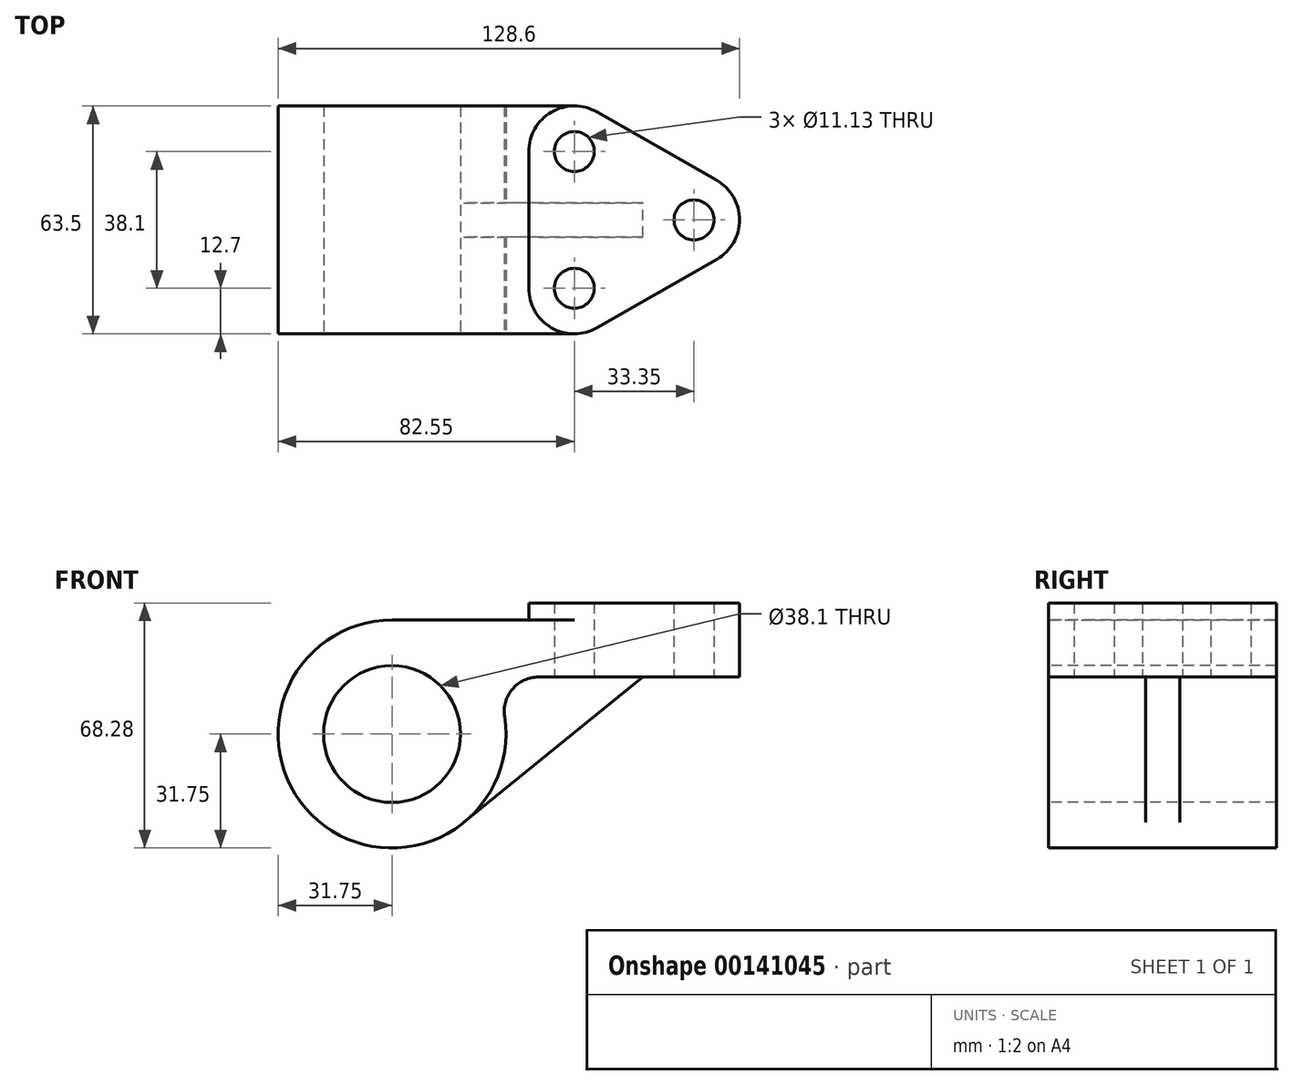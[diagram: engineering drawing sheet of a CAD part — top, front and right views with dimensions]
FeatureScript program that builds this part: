
annotation { "Feature Type Name" : "Feature", "Feature Type Description" : "" }
export const myFeature = defineFeature(function(context is Context, id is Id, definition is map)
    precondition{}
    {
        {
            var Q0;
            Q0=qCreatedBy(makeId("Front.planeOp"),FACE);
            var sketch = newSketch(context, id + "F0", { "sketchPlane" : qUnion([Q0])});
            skCircle(sketch, "E0", {"center": v(0, 0) * mm, "radius": 19.05 * mm});
            skCircle(sketch, "E1", {"center": v(0, 0) * mm, "radius": 31.75 * mm});
            skLineSegment(sketch, "E2", {"start": v(0, 31.75) * mm, "end": v(50.8, 31.75) * mm});
            skLineSegment(sketch, "E3", {"start": v(50.8, 31.75) * mm, "end": v(50.8, 15.87) * mm});
            skLineSegment(sketch, "E4", {"start": v(50.8, 15.87) * mm, "end": v(27.5, 15.87) * mm});
            skSolve(sketch);
        }
        {
            var Q0;
            Q0=qSketchRegion(id+"F0",true);
            extrude(context, id + "F1", {"entities" : qUnion([Q0]), "endBound" : BoundingType.SYMMETRIC, "oppositeDirection" : true, "depth" : 63.5 * mm});
        }
        {
            var Q0;
            Q0=makeQuery(id+"F1.opExtrude","SWEPT_FACE",FACE,{"disambiguationData":[OSD([sQuery(id+"F0.wireOp",EDGE,"E4")])]});
            var sketch = newSketch(context, id + "F2", { "sketchPlane" : qUnion([Q0])});
            skCircle(sketch, "E5", {"center": v(50.8, 19.05) * mm, "radius": 5.56 * mm});
            skCircle(sketch, "E6", {"center": v(50.8, -19.05) * mm, "radius": 5.56 * mm});
            skCircle(sketch, "E7", {"center": v(84.15, 0) * mm, "radius": 5.56 * mm});
            skLineSegment(sketch, "E8", {"start": v(50.8, 31.75) * mm, "end": v(27.5, 31.75) * mm, "construction": true});
            skLineSegment(sketch, "E9", {"start": v(27.5, 31.75) * mm, "end": v(27.5, -31.75) * mm, "construction": true});
            skLineSegment(sketch, "E10", {"start": v(27.5, -31.75) * mm, "end": v(50.8, -31.75) * mm, "construction": true});
            skLineSegment(sketch, "E11", {"start": v(50.8, -31.75) * mm, "end": v(50.8, 31.75) * mm, "construction": true});
            skArc(sketch, "E12", {"start": v(57.1, 30.08) * mm, "mid": v(44.42, 30.03) * mm, "end": v(38.1, 19.05) * mm});
            skArc(sketch, "E13", {"start": v(90.45, -11.03) * mm, "mid": v(96.85, 0) * mm, "end": v(90.45, 11.03) * mm});
            skArc(sketch, "E14", {"start": v(38.1, -19.05) * mm, "mid": v(44.42, -30.03) * mm, "end": v(57.1, -30.08) * mm});
            skLineSegment(sketch, "E15", {"start": v(57.1, 30.08) * mm, "end": v(90.45, 11.03) * mm});
            skLineSegment(sketch, "E16", {"start": v(90.45, -11.03) * mm, "end": v(57.1, -30.08) * mm});
            skLineSegment(sketch, "E17", {"start": v(38.1, 19.05) * mm, "end": v(38.1, -19.05) * mm});
            skSolve(sketch);
        }
        {
            var Q0;
            Q0=qSketchRegion(id+"F2",true);
            extrude(context, id + "F3", {"entities" : qUnion([Q0]), "operationType" : NewBodyOperationType.ADD, "oppositeDirection" : true, "depth" : 20.65 * mm});
        }
        {
            var Q0;
            Q0=makeQuery(id+"F1.opExtrude","SWEPT_EDGE",EDGE,{"disambiguationData":[OSD([sQuery(id+"F0.wireOp",EDGE,"E1"),sQuery(id+"F0.wireOp",EDGE,"E4")])]});
            fillet(context, id + "F4", {"entities" : qUnion([Q0]), "radius" : 9.52 * mm, "tangentPropagation" : true, "allowEdgeOverflow" : false});
        }
        {
            var Q0;
            Q0=qCreatedBy(makeId("Front.planeOp"),FACE);
            var sketch = newSketch(context, id + "F5", { "sketchPlane" : qUnion([Q0])});
            skLineSegment(sketch, "E18", {"start": v(69.85, 15.88) * mm, "end": v(20.03, -24.63) * mm});
            skArc(sketch, "E19.0", {"start": v(20.03, -24.63) * mm, "mid": v(29.64, -11.39) * mm, "end": v(31.37, 4.88) * mm});
            skArc(sketch, "E19.1", {"start": v(31.37, 4.88) * mm, "mid": v(33.55, 12.55) * mm, "end": v(40.78, 15.87) * mm});
            skLineSegment(sketch, "E19.2", {"start": v(50.8, 15.87) * mm, "end": v(40.78, 15.87) * mm});
            skLineSegment(sketch, "E19.3", {"start": v(57.1, 15.88) * mm, "end": v(50.8, 15.88) * mm});
            skLineSegment(sketch, "E19.4", {"start": v(57.1, 15.88) * mm, "end": v(69.85, 15.88) * mm});
            skPoint(sketch, "E20", {"position": v(20.03, -24.63) * mm});
            skPoint(sketch, "E21", {"position": v(69.85, 15.88) * mm});
            skPoint(sketch, "E22.orphan", {"position": v(0, 31.75) * mm});
            skPoint(sketch, "E23.orphan", {"position": v(90.45, 15.88) * mm});
            skSolve(sketch);
        }
        {
            var Q0;
            Q0=qSketchRegion(id+"F5",true);
            extrude(context, id + "F6", {"entities" : qUnion([Q0]), "operationType" : NewBodyOperationType.ADD, "endBound" : BoundingType.SYMMETRIC, "depth" : 9.52 * mm});
        }
        {
            var Q0;
            Q0=makeQuery(id+"F3.opExtrude","CAP_FACE",FACE,{"disambiguationData":[OSD([sQuery(id+"F2.wireOp",EDGE,"E5"),sQuery(id+"F2.wireOp",EDGE,"E6"),sQuery(id+"F2.wireOp",EDGE,"E7"),sQuery(id+"F2.wireOp",EDGE,"E12"),sQuery(id+"F2.wireOp",EDGE,"E13"),sQuery(id+"F2.wireOp",EDGE,"E14"),sQuery(id+"F2.wireOp",EDGE,"E15"),sQuery(id+"F2.wireOp",EDGE,"E16"),sQuery(id+"F2.wireOp",EDGE,"E17")])],"isStart":false});
            var sketch = newSketch(context, id + "F7", { "sketchPlane" : qUnion([Q0])});
            skCircle(sketch, "E24.0", {"center": v(50.8, 19.05) * mm, "radius": 5.56 * mm});
            skCircle(sketch, "E25.0", {"center": v(50.8, -19.05) * mm, "radius": 5.56 * mm});
            skSolve(sketch);
        }
        {
            var Q0;
            Q0=qSketchRegion(id+"F7",true);
            extrude(context, id + "F8", {"entities" : qUnion([Q0]), "operationType" : NewBodyOperationType.REMOVE, "endBound" : BoundingType.THROUGH_ALL, "oppositeDirection" : true, "depth" : 25.4 * mm});
        }
    });
